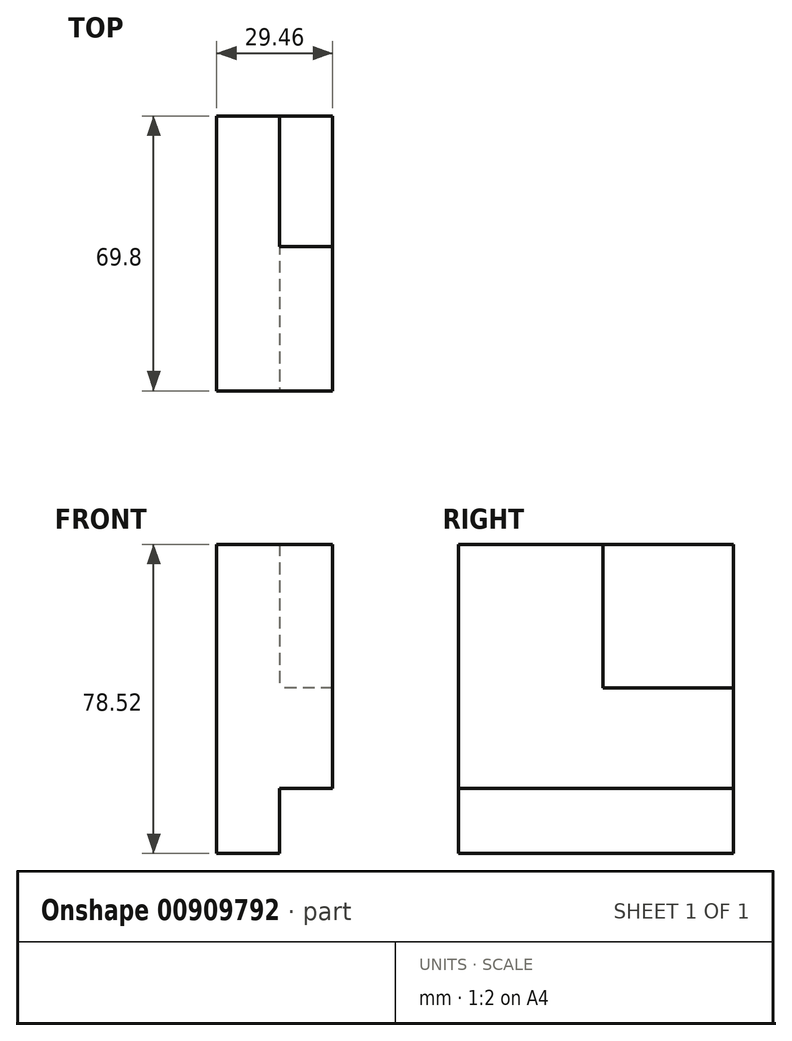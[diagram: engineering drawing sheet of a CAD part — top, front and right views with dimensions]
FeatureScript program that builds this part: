
annotation { "Feature Type Name" : "Feature", "Feature Type Description" : "" }
export const myFeature = defineFeature(function(context is Context, id is Id, definition is map)
    precondition{}
    {
        {
            var Q0;
            Q0=qCreatedBy(makeId("Right.planeOp"),FACE);
            var sketch = newSketch(context, id + "F0", { "sketchPlane" : qUnion([Q0])});
            skLineSegment(sketch, "E0", {"start": v(-36.62, 50.74) * mm, "end": v(-36.62, -27.78) * mm});
            skLineSegment(sketch, "E1", {"start": v(-36.62, -27.78) * mm, "end": v(33.18, -27.78) * mm});
            skLineSegment(sketch, "E2", {"start": v(33.18, -27.78) * mm, "end": v(33.18, 50.74) * mm});
            skLineSegment(sketch, "E3", {"start": v(33.18, 50.74) * mm, "end": v(-36.62, 50.74) * mm});
            skSolve(sketch);
        }
        {
            var Q0;
            Q0=makeQuery(id+"F0.imprint","IMPRINT",FACE,{"disambiguationData":[TD([[makeQuery(id+"F0.imprint","IMPRINT",EDGE,{"derivedFrom":sQuery(id+"F0.wireOp",EDGE,"E0")}),1.0]])]});
            extrude(context, id + "F1", {"entities" : qUnion([Q0]), "depth" : 16 * mm, "offsetDistance" : 25.4 * mm});
        }
        {
            var Q0;
            Q0=makeQuery(id+"F1.opExtrude","CAP_FACE",FACE,{"disambiguationData":[OSD([sQuery(id+"F0.wireOp",EDGE,"E0"),sQuery(id+"F0.wireOp",EDGE,"E1"),sQuery(id+"F0.wireOp",EDGE,"E2"),sQuery(id+"F0.wireOp",EDGE,"E3")])],"isStart":false});
            var sketch = newSketch(context, id + "F2", { "sketchPlane" : qUnion([Q0])});
            skLineSegment(sketch, "E4", {"start": v(0, 50.74) * mm, "end": v(0, 14.23) * mm});
            skPoint(sketch, "E4.startSnap0", {"position": v(-1.72, 50.74) * mm});
            skLineSegment(sketch, "E5", {"start": v(0, 14.23) * mm, "end": v(33.18, 14.23) * mm});
            skLineSegment(sketch, "E6", {"start": v(33.18, 14.23) * mm, "end": v(33.18, -11.25) * mm});
            skLineSegment(sketch, "E7", {"start": v(33.18, -11.25) * mm, "end": v(-36.62, -11.25) * mm});
            skLineSegment(sketch, "E8", {"start": v(-36.62, -11.25) * mm, "end": v(-36.62, 50.74) * mm});
            skLineSegment(sketch, "E9", {"start": v(-36.62, 50.74) * mm, "end": v(0, 50.74) * mm});
            skSolve(sketch);
        }
        {
            var Q0;
            Q0 = qSketchRegion(id + "F2", true);
            extrude(context, id + "F3", {"entities" : qUnion([Q0]), "operationType" : NewBodyOperationType.ADD, "depth" : 13.46 * mm, "offsetDistance" : 25.4 * mm});
        }
    });
